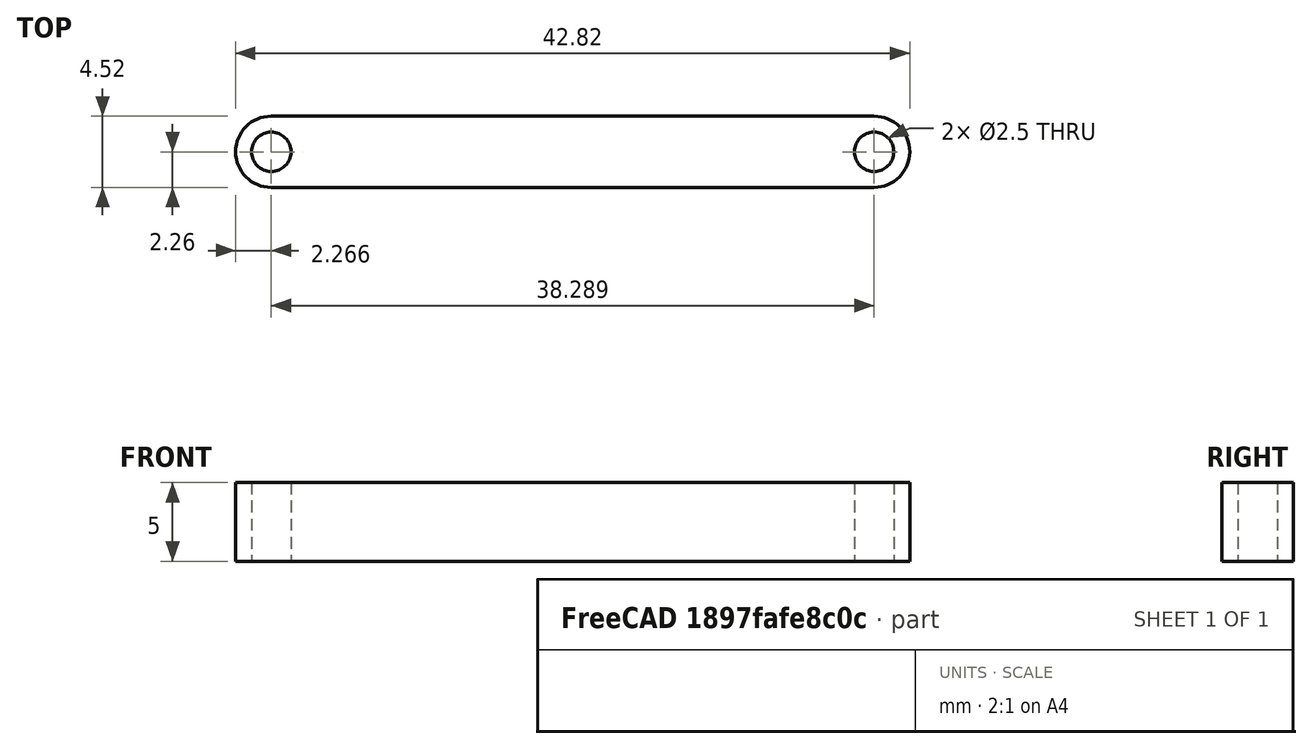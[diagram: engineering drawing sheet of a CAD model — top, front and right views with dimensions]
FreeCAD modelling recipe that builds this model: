
FCSTD DOCUMENT  (FreeCAD 0.19R24291 (Git))
Label: FBR_defLink_Scaled
License: All rights reserved
LicenseURL: http://en.wikipedia.org/wiki/All_rights_reserved
objects: Sketcher::SketchObject×1, PartDesign::Pad×1, PartDesign::Hole×1, PartDesign::Body×1, Part::FeaturePython×1
note: 7 computed .brp shape members not serialized (recipe doc carries the construction recipe); baked Part::Feature solids carry a one-line shape summary decoded from their .brp

FEATURE [Sketcher::SketchObject] Sketch
  FullyConstrained = false
  MapMode = 5
  Support = -> [XY_Plane004]
  sketch-geometry (4):
    g0: ArcOfCircle CenterX=-36.2276 CenterY=0 CenterZ=0 NormalX=0 NormalY=0 NormalZ=1 AngleXU=0 Radius=4.52517 StartAngle=1.5708 EndAngle=4.71239
    g1: ArcOfCircle CenterX=40.3501 CenterY=4e-16 CenterZ=0 NormalX=0 NormalY=0 NormalZ=1 AngleXU=0 Radius=4.52517 StartAngle=4.71239 EndAngle=7.85398
    g2: LineSegment StartX=-36.2276 StartY=-4.52517 StartZ=0 EndX=40.3501 EndY=-4.52517 EndZ=0
    g3: LineSegment StartX=-36.2276 StartY=4.52517 StartZ=0 EndX=40.3501 EndY=4.52517 EndZ=0
  constraints (7):
    c: Tangent(g0,g3) = 1.5708
    c: Tangent(g0,g2) = -1.5708
    c: Tangent(g2,g1) = -1.5708
    c: Tangent(g3,g1) = 1.5708
    c: Horizontal(g2)
    c: Equal(g0,g1)
    c: PointOnObject(g0,g-1)
FEATURE [PartDesign::Pad] Pad002
  Direction = (1,1,1)
  Length = 10
  Length2 = 100
  Profile = -> Sketch
  Type = 0
FEATURE [PartDesign::Hole] Hole
  BaseFeature = -> Pad002
  Depth = 25
  DepthType = 0
  Diameter = 5
  DrillForDepth = false
  DrillPoint = 1
  DrillPointAngle = 118
  HoleCutCountersinkAngle = 90
  HoleCutCustomValues = false
  HoleCutDepth = 0
  HoleCutDiameter = 6.1
  HoleCutType = 0
  ModelActualThread = false
  Profile = -> Pad002 [Face6]
  Tapered = false
  TaperedAngle = 90
  ThreadAngle = 0
  ThreadClass = 0
  ThreadCutOffInner = 0
  ThreadCutOffOuter = 0
  ThreadDirection = 0
  ThreadFit = 0
  ThreadPitch = 0
  ThreadSize = 0
  ThreadType = 0
  Threaded = false
FEATURE [PartDesign::Body] Body004  label="def_Link"
  Group = -> [Sketch,Pad002,Hole]
  Origin = -> Origin004
  Tip = -> Hole
FEATURE [Part::FeaturePython] Clone015  label="def_Link006_SampleScaled"  # Draft clone (typed FeaturePython)
  AttacherType = Attacher::AttachEngine3D
  Fuse = false
  Objects = -> [Body004]
  Scale = (0.5,0.5,0.5)
